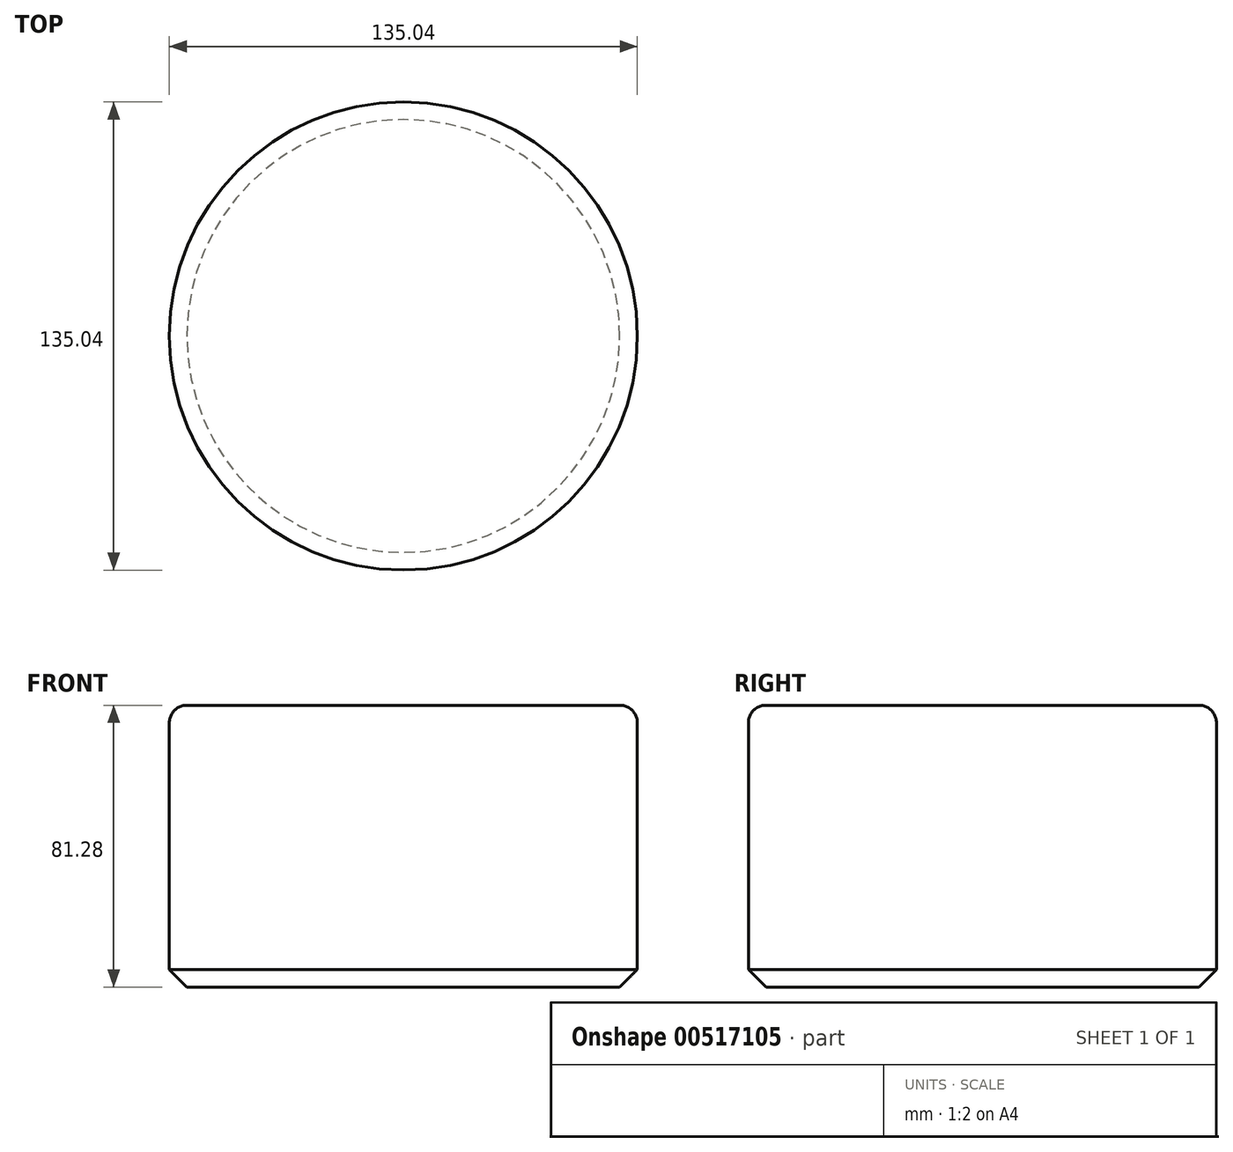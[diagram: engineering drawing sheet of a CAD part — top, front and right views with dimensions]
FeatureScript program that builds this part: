
annotation { "Feature Type Name" : "Feature", "Feature Type Description" : "" }
export const myFeature = defineFeature(function(context is Context, id is Id, definition is map)
    precondition{}
    {
        {
            var Q0;
            Q0=qCreatedBy(makeId("Top.planeOp"),FACE);
            var sketch = newSketch(context, id + "F0", { "sketchPlane" : qUnion([Q0])});
            skCircle(sketch, "E0", {"center": v(0, 0) * mm, "radius": 67.52 * mm});
            skSolve(sketch);
        }
        {
            var Q0;
            Q0 = qSketchRegion(id + "F0", true);
            extrude(context, id + "F1", {"entities" : qUnion([Q0]), "depth" : 81.28 * mm, "offsetDistance" : 25.4 * mm});
        }
        {
            var Q0;
            Q0=makeQuery(id+"F1.opExtrude","CAP_EDGE",EDGE,{"disambiguationData":[OSD([sQuery(id+"F0.wireOp",EDGE,"E0")])],"isStart":false});
            fillet(context, id + "F2", {"entities" : qUnion([Q0]), "radius" : 5.08 * mm, "tangentPropagation" : true, "allowEdgeOverflow" : false});
        }
        {
            var Q0;
            Q0=makeQuery(id+"F1.opExtrude","CAP_EDGE",EDGE,{"disambiguationData":[OSD([sQuery(id+"F0.wireOp",EDGE,"E0")])],"isStart":true});
            chamfer(context, id + "F3", {"entities" : qUnion([Q0]), "width" : 5.08 * mm, "tangentPropagation" : true});
        }
    });
